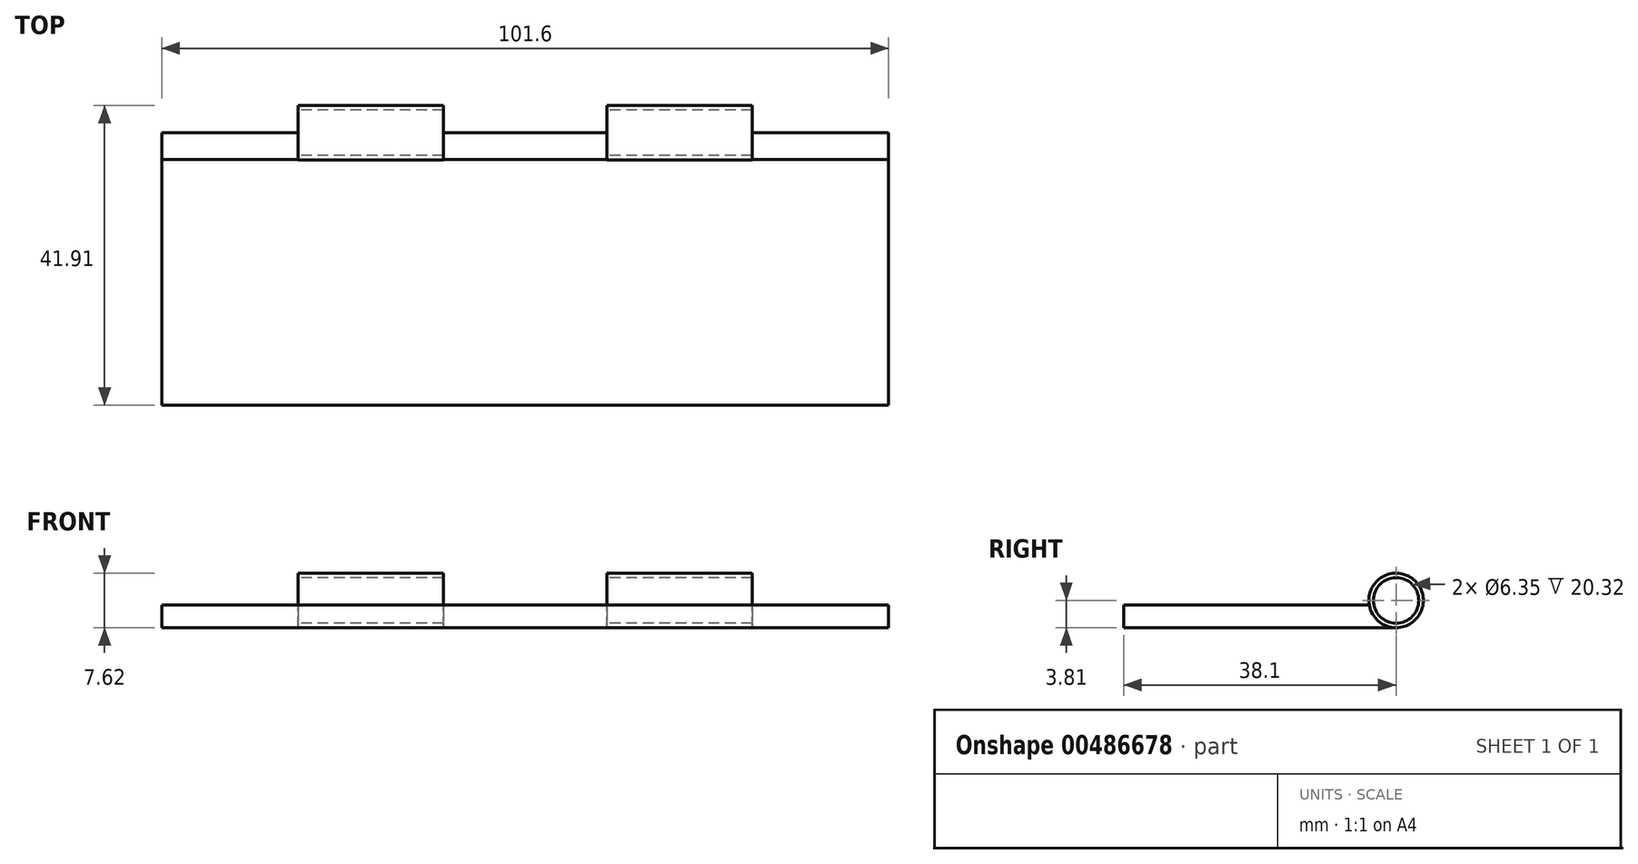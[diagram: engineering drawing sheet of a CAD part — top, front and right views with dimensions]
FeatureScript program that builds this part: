
annotation { "Feature Type Name" : "Feature", "Feature Type Description" : "" }
export const myFeature = defineFeature(function(context is Context, id is Id, definition is map)
    precondition{}
    {
        {
            var Q0;
            Q0=qCreatedBy(makeId("Top.planeOp"),FACE);
            var sketch = newSketch(context, id + "F0", { "sketchPlane" : qUnion([Q0])});
            skLineSegment(sketch, "E0.bottom", {"start": v(0, 0) * mm, "end": v(-101.6, 0) * mm});
            skLineSegment(sketch, "E0.top", {"start": v(0, -38.1) * mm, "end": v(-101.6, -38.1) * mm});
            skLineSegment(sketch, "E0.left", {"start": v(0, 0) * mm, "end": v(0, -38.1) * mm});
            skLineSegment(sketch, "E0.right", {"start": v(-101.6, 0) * mm, "end": v(-101.6, -38.1) * mm});
            skSolve(sketch);
        }
        {
            var Q0;
            Q0=qSketchRegion(id+"F0",true);
            extrude(context, id + "F1", {"entities" : qUnion([Q0]), "depth" : 3.17 * mm});
        }
        {
            var Q0;
            Q0=makeQuery(id+"F1.opExtrude","SWEPT_FACE",FACE,{"disambiguationData":[OSD([sQuery(id+"F0.wireOp",EDGE,"E0.right")])]});
            var sketch = newSketch(context, id + "F2", { "sketchPlane" : qUnion([Q0])});
            skCircle(sketch, "E1", {"center": v(0, 3.81) * mm, "radius": 3.81 * mm});
            skCircle(sketch, "E2", {"center": v(0, 3.81) * mm, "radius": 3.18 * mm});
            skSolve(sketch);
        }
        {
            var Q0;
            {var subQ0=sQuery(id+"F2.wireOp",EDGE,"E1");var subQ1=sQuery(id+"F0.wireOp",EDGE,"E0.right");var subQ4=makeQuery(id+"F1.opExtrude","CAP_EDGE",EDGE,{"disambiguationData":[OSD([subQ1])],"isStart":false});var subQ5=makeQuery(id+"F2.imprint","INTERSECT",VERTEX,{"derivedFrom":[subQ4,subQ0]});Q0=makeQuery(id+"F2.imprint","IMPRINT",FACE,{"disambiguationData":[TD([[makeQuery(id+"F2.imprint","IMPRINT",EDGE,{"disambiguationData":[TD([[subQ5,1.0]])],"derivedFrom":subQ4}),1.0]])]});}
            var Q1;
            {var subQ0=sQuery(id+"F2.wireOp",EDGE,"E1");var subQ1=sQuery(id+"F0.wireOp",EDGE,"E0.right");var subQ4=makeQuery(id+"F1.opExtrude","CAP_EDGE",EDGE,{"disambiguationData":[OSD([subQ1])],"isStart":false});var subQ5=makeQuery(id+"F2.imprint","INTERSECT",VERTEX,{"derivedFrom":[subQ4,subQ0]});Q1=makeQuery(id+"F2.imprint","IMPRINT",FACE,{"disambiguationData":[TD([[makeQuery(id+"F2.imprint","IMPRINT",EDGE,{"disambiguationData":[TD([[subQ5,1.0]])],"derivedFrom":subQ4}),-1.0]])]});}
            var Q2;
            {var subQ0=sQuery(id+"F2.wireOp",EDGE,"E2");var subQ1=sQuery(id+"F0.wireOp",EDGE,"E0.right");var subQ4=makeQuery(id+"F1.opExtrude","CAP_EDGE",EDGE,{"disambiguationData":[OSD([subQ1])],"isStart":false});var subQ5=makeQuery(id+"F2.imprint","INTERSECT",VERTEX,{"derivedFrom":[subQ4,subQ0]});Q2=makeQuery(id+"F2.imprint","IMPRINT",FACE,{"disambiguationData":[TD([[makeQuery(id+"F2.imprint","IMPRINT",EDGE,{"disambiguationData":[TD([[subQ5,1.0]])],"derivedFrom":subQ0}),1.0]])]});}
            var Q3;
            Q3=makeQuery(id+"F1.opExtrude","SWEPT_FACE",FACE,{"disambiguationData":[OSD([sQuery(id+"F0.wireOp",EDGE,"E0.left")])]});
            extrude(context, id + "F3", {"entities" : qUnion([Q0, Q1, Q2]), "operationType" : NewBodyOperationType.REMOVE, "oppositeDirection" : true, "endBoundEntityFace" : qUnion([Q3]), "depth" : 254 * mm});
        }
        {
            var Q0;
            Q0=qSketchRegion(id+"F2",true);
            var Q1;
            Q1=makeQuery(id+"F1.opExtrude","SWEPT_FACE",FACE,{"disambiguationData":[OSD([sQuery(id+"F0.wireOp",EDGE,"E0.left")])]});
            extrude(context, id + "F4", {"entities" : qUnion([Q0]), "operationType" : NewBodyOperationType.ADD, "endBound" : BoundingType.UP_TO_SURFACE, "oppositeDirection" : true, "endBoundEntityFace" : qUnion([Q1]), "depth" : 25.4 * mm});
        }
        {
            var Q0;
            Q0=qSketchRegion(id+"F2",true);
            extrude(context, id + "F5", {"entities" : qUnion([Q0]), "operationType" : NewBodyOperationType.REMOVE, "oppositeDirection" : true, "depth" : 19.05 * mm});
        }
        {
            var Q0;
            Q0=qSketchRegion(id+"F2",true);
            extrude(context, id + "F6", {"entities" : qUnion([Q0]), "operationType" : NewBodyOperationType.REMOVE, "oppositeDirection" : true, "depth" : 62.23 * mm, "hasSecondDirection" : true, "secondDirectionOppositeDirection" : true, "secondDirectionDepth" : 39.37 * mm});
        }
        {
            var Q0;
            Q0=qSketchRegion(id+"F2",true);
            extrude(context, id + "F7", {"entities" : qUnion([Q0]), "operationType" : NewBodyOperationType.REMOVE, "oppositeDirection" : true, "depth" : 101.6 * mm, "hasSecondDirection" : true, "secondDirectionOppositeDirection" : true, "secondDirectionDepth" : 82.55 * mm});
        }
    });
